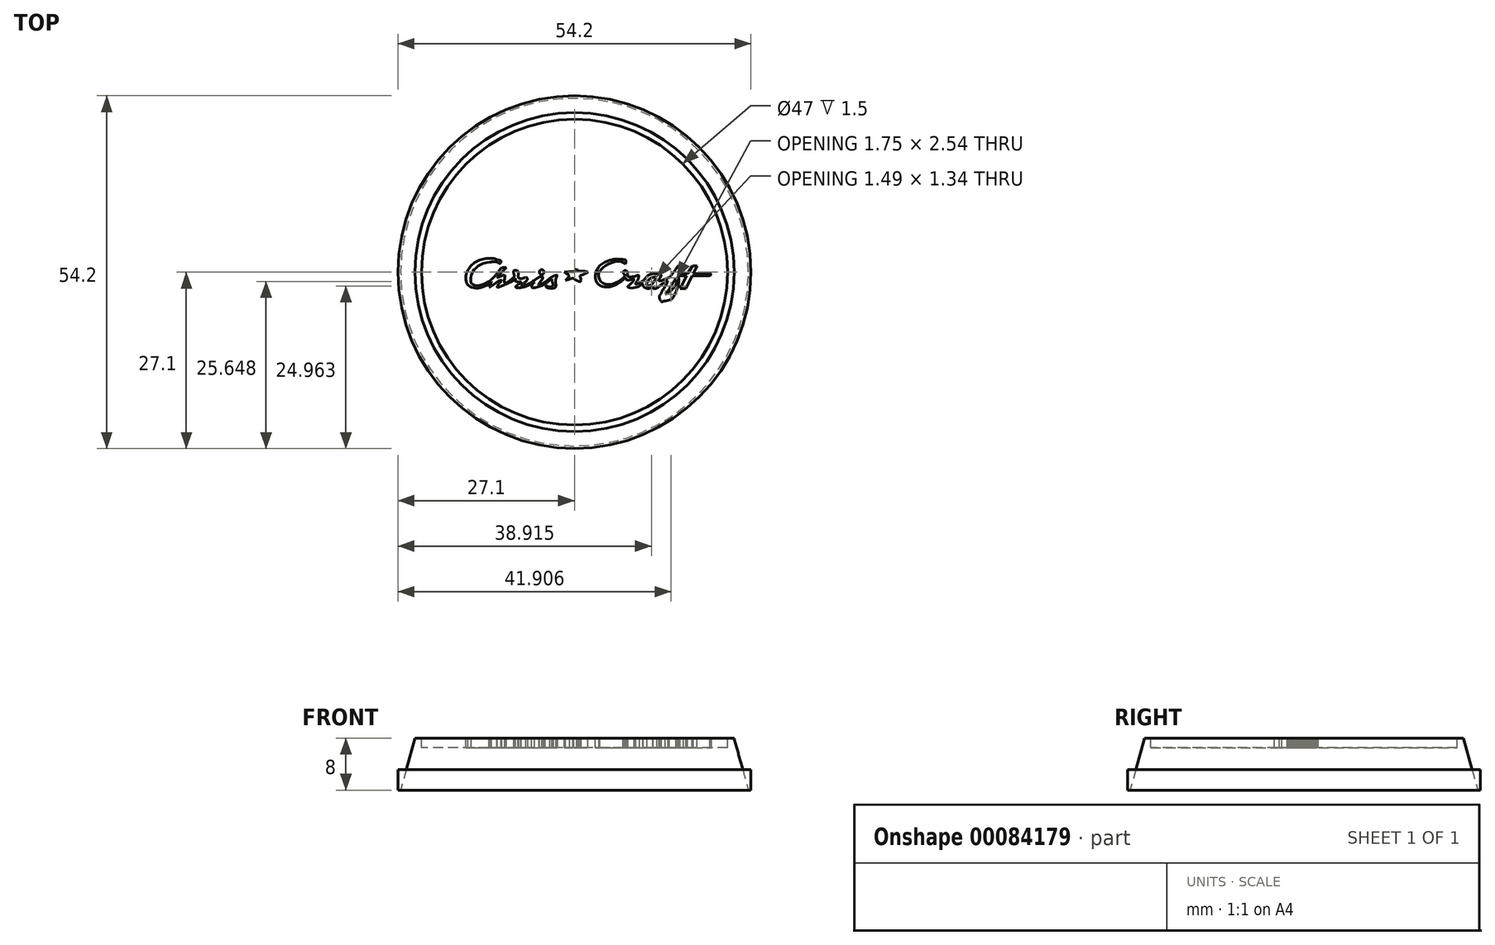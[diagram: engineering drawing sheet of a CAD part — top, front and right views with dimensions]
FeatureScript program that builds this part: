
annotation { "Feature Type Name" : "Feature", "Feature Type Description" : "" }
export const myFeature = defineFeature(function(context is Context, id is Id, definition is map)
    precondition{}
    {
        {
            var Q0;
            Q0=qCreatedBy(makeId("Top.planeOp"),FACE);
            var sketch = newSketch(context, id + "F0", { "sketchPlane" : qUnion([Q0])});
            skCircle(sketch, "E0", {"center": v(0, 0) * mm, "radius": 26.7 * mm});
            skSolve(sketch);
        }
        {
            var Q0;
            Q0=makeQuery(id+"F0.imprint","IMPRINT",FACE,{"disambiguationData":[TD([[makeQuery(id+"F0.imprint","IMPRINT",EDGE,{"derivedFrom":sQuery(id+"F0.wireOp",EDGE,"E0")}),1.0]])]});
            cPlane(context, id + "F1", {"entities" : qUnion([Q0]), "cplaneType" : CPlaneType.OFFSET, "offset" : 8 * mm, "width" : 150 * mm, "height" : 150 * mm});
        }
        {
            var Q0;
            Q0=qCreatedBy(id+"F1.planeOp",FACE);
            var sketch = newSketch(context, id + "F2", { "sketchPlane" : qUnion([Q0])});
            skCircle(sketch, "E1", {"center": v(0, 0) * mm, "radius": 24.5 * mm});
            skSolve(sketch);
        }
        {
            var Q0;
            Q0=makeQuery(id+"F0.imprint","IMPRINT",FACE,{"disambiguationData":[TD([[makeQuery(id+"F0.imprint","IMPRINT",EDGE,{"derivedFrom":sQuery(id+"F0.wireOp",EDGE,"E0")}),1.0]])]});
            var Q1;
            Q1=makeQuery(id+"F2.imprint","IMPRINT",FACE,{"disambiguationData":[TD([[makeQuery(id+"F2.imprint","IMPRINT",EDGE,{"derivedFrom":sQuery(id+"F2.wireOp",EDGE,"E1")}),1.0]])]});
            loft(context, id + "F3", {"sheetProfilesArray" : [{ "sheetProfileEntities" : qUnion([Q0]) }, { "sheetProfileEntities" : qUnion([Q1]) }]});
        }
        {
            var Q0;
            Q0=makeQuery(id+"F3.opLoft","CAP_FACE",FACE,{"disambiguationData":[OSD([makeQuery(id+"F2.imprint","IMPRINT",FACE,{"disambiguationData":[TD([[makeQuery(id+"F2.imprint","IMPRINT",EDGE,{"derivedFrom":sQuery(id+"F2.wireOp",EDGE,"E1")}),1.0]])]})])],"isStart":true});
            cPlane(context, id + "F4", {"entities" : qUnion([Q0]), "cplaneType" : CPlaneType.OFFSET, "offset" : 0 * mm, "width" : 150 * mm, "height" : 150 * mm});
        }
        {
            var Q0;
            Q0=qCreatedBy(id+"F4.planeOp",FACE);
            var sketch = newSketch(context, id + "F5", { "sketchPlane" : qUnion([Q0])});
            skCircle(sketch, "E2", {"center": v(0, 0) * mm, "radius": 23.5 * mm});
            skSolve(sketch);
        }
        {
            var Q0;
            Q0=makeQuery(id+"F5.imprint","IMPRINT",FACE,{"disambiguationData":[TD([[makeQuery(id+"F5.imprint","IMPRINT",EDGE,{"derivedFrom":sQuery(id+"F5.wireOp",EDGE,"E2")}),1.0]])]});
            extrude(context, id + "F6", {"entities" : qUnion([Q0]), "operationType" : NewBodyOperationType.REMOVE, "oppositeDirection" : true, "depth" : 1.5 * mm});
        }
        {
            var Q0;
            Q0=makeQuery(id+"F3.opLoft","CAP_FACE",FACE,{"disambiguationData":[OSD([makeQuery(id+"F0.imprint","IMPRINT",FACE,{"disambiguationData":[TD([[makeQuery(id+"F0.imprint","IMPRINT",EDGE,{"derivedFrom":sQuery(id+"F0.wireOp",EDGE,"E0")}),1.0]])]})])],"isStart":true});
            cPlane(context, id + "F7", {"entities" : qUnion([Q0]), "cplaneType" : CPlaneType.OFFSET, "offset" : 6.5 * mm, "oppositeDirection" : true, "width" : 150 * mm, "height" : 150 * mm});
        }
        {
            var Q0;
            Q0=qCreatedBy(id+"F7.planeOp",FACE);
            cPlane(context, id + "F8", {"entities" : qUnion([Q0]), "cplaneType" : CPlaneType.OFFSET, "offset" : 0 * mm, "width" : 150 * mm, "height" : 150 * mm});
        }
        {
            var Q0;
            Q0=qCreatedBy(id+"F1.planeOp",FACE);
            var sketch = newSketch(context, id + "F9", { "sketchPlane" : qUnion([Q0])});
            skPoint(sketch, "E3.end.orphan", {"position": v(217.76, 2.1) * mm});
            skFitSpline(sketch, "E4", {"points": [v(-16.36, 0.32) * mm, v(-15.75, 1.13) * mm, v(-14.75, 1.75) * mm, v(-13.66, 2.07) * mm, v(-12.5, 2.09) * mm, v(-11.62, 1.85) * mm, v(-11.25, 1.79) * mm], "startDerivative": vector(4.48, 6.5) * mm, "endDerivative": vector(2.92, -0.63) * mm});
            skFitSpline(sketch, "E5", {"points": [v(-11.25, 1.79) * mm, v(-11.45, 1.32) * mm, v(-11.8, 1.48) * mm, v(-12.14, 1.6) * mm, v(-13.06, 1.53) * mm], "startDerivative": vector(-0.58, -2.65) * mm, "endDerivative": vector(-3.08, -0.28) * mm});
            skFitSpline(sketch, "E6", {"points": [v(-16.36, 0.32) * mm, v(-16.62, -0.3) * mm, v(-16.62, -1.49) * mm, v(-16.1, -2.2) * mm, v(-14.71, -2.44) * mm, v(-13.23, -1.87) * mm, v(-12.73, -1.47) * mm], "startDerivative": vector(-2.23, -3.97) * mm, "endDerivative": vector(3.52, 2.36) * mm});
            skFitSpline(sketch, "E7", {"points": [v(-13.06, 1.53) * mm, v(-13.79, 1.4) * mm, v(-14.93, 0.83) * mm, v(-15.64, 0) * mm, v(-15.9, -0.75) * mm, v(-15.9, -1.59) * mm, v(-15.62, -1.89) * mm, v(-14.7, -2.06) * mm, v(-13.23, -1.5) * mm, v(-12.83, -1.18) * mm], "startDerivative": vector(-9.92, -1.24) * mm, "endDerivative": vector(3.94, 3.33) * mm});
            skFitSpline(sketch, "E8", {"points": [v(-12.83, -1.18) * mm, v(-11.73, 0) * mm, v(-11.25, 0.62) * mm, v(-10.44, 0.68) * mm], "startDerivative": vector(3.02, 2.92) * mm, "endDerivative": vector(3.06, -0.25) * mm});
            skFitSpline(sketch, "E9", {"points": [v(-10.44, 0.68) * mm, v(-11.19, 0) * mm, v(-11.9, -0.87) * mm], "startDerivative": vector(-1.56, -1.33) * mm, "endDerivative": vector(-1.34, -1.77) * mm});
            skFitSpline(sketch, "E10", {"points": [v(-12.73, -1.47) * mm, v(-13.11, -2.26) * mm], "startDerivative": vector(-0.49, -0.89) * mm, "endDerivative": vector(-0.49, -0.89) * mm});
            skFitSpline(sketch, "E11", {"points": [v(-13.11, -2.26) * mm, v(-12.9, -2.26) * mm, v(-11.64, -1.36) * mm, v(-11.23, -1.27) * mm, v(-11.87, -2.26) * mm, v(-9.33, -1.19) * mm], "startDerivative": vector(2.54, -0.83) * mm, "endDerivative": vector(12.1, 7) * mm});
            skFitSpline(sketch, "E12", {"points": [v(-11.9, -0.87) * mm, v(-11.17, -0.56) * mm], "startDerivative": vector(0.72, 0.31) * mm, "endDerivative": vector(0.72, 0.31) * mm});
            skFitSpline(sketch, "E13", {"points": [v(-11.17, -0.56) * mm, v(-10.7, -0.56) * mm, v(-10.75, -1.61) * mm, v(-9.74, -1.13) * mm, v(-9.18, -0.56) * mm], "startDerivative": vector(3.38, 1.13) * mm, "endDerivative": vector(1.67, 2.1) * mm});
            skFitSpline(sketch, "E14", {"points": [v(-9.18, -0.56) * mm, v(-9.32, -0.29) * mm, v(-9.32, 0.17) * mm, v(-8.84, 0.25) * mm, v(-8.64, -0.14) * mm, v(-8.68, -0.56) * mm, v(-9.03, -0.96) * mm, v(-9.33, -1.19) * mm], "startDerivative": vector(-1.19, 1.93) * mm, "endDerivative": vector(-3.2, -1.17) * mm});
            skFitSpline(sketch, "E15", {"points": [v(-8.68, -0.56) * mm, v(-8.5, -0.96) * mm, v(-7.91, -0.96) * mm, v(-7.49, -0.77) * mm], "startDerivative": vector(0.37, -1.64) * mm, "endDerivative": vector(1.59, 0.59) * mm});
            skFitSpline(sketch, "E16", {"points": [v(-7.49, -0.77) * mm, v(-7.22, -1.06) * mm, v(-7.9, -1.84) * mm, v(-8.22, -2.06) * mm], "startDerivative": vector(1.51, -0.83) * mm, "endDerivative": vector(-0.95, -0.54) * mm});
            skFitSpline(sketch, "E17", {"points": [v(-9.03, -0.96) * mm, v(-9.03, -1.42) * mm, v(-8.18, -1.55) * mm, v(-9.03, -2.22) * mm, v(-8.26, -2.4) * mm, v(-6.15, -1.52) * mm], "startDerivative": vector(-1.52, -4.12) * mm, "endDerivative": vector(6.97, 4) * mm});
            skFitSpline(sketch, "E18", {"points": [v(-8.22, -2.06) * mm, v(-8.13, -2.18) * mm, v(-7.19, -1.87) * mm, v(-6.39, -1.4) * mm, v(-5.86, -1.05) * mm, v(-5.42, -0.74) * mm, v(-5.12, -0.66) * mm, v(-4.87, -0.75) * mm, v(-5.02, -1.22) * mm], "startDerivative": vector(0.53, -2.89) * mm, "endDerivative": vector(-2.38, -4.4) * mm});
            skFitSpline(sketch, "E19.trimOffspring", {"points": [v(-9.18, -0.56) * mm, v(-9.32, -0.29) * mm, v(-9.32, 0.17) * mm, v(-8.84, 0.25) * mm, v(-8.64, -0.14) * mm, v(-8.68, -0.56) * mm, v(-9.03, -0.96) * mm, v(-9.33, -1.19) * mm], "startDerivative": vector(-1.19, 1.93) * mm, "endDerivative": vector(-3.2, -1.17) * mm});
            skFitSpline(sketch, "E20", {"points": [v(-6.15, -1.52) * mm, v(-6.54, -2.06) * mm, v(-6.49, -2.37) * mm, v(-5.58, -2.27) * mm, v(-4.46, -1.78) * mm, v(-3.82, -1.22) * mm], "startDerivative": vector(-2.62, -2.83) * mm, "endDerivative": vector(2.76, 2.7) * mm});
            skFitSpline(sketch, "E21", {"points": [v(-5.02, -1.22) * mm, v(-5.51, -1.95) * mm, v(-4.88, -1.76) * mm, v(-3.93, -1.1) * mm, v(-3.47, -0.75) * mm, v(-3.16, -0.57) * mm, v(-2.9, -0.5) * mm, v(-2.68, -0.5) * mm, v(-2.77, -0.81) * mm, v(-2.91, -1.22) * mm, v(-2.86, -2.06) * mm, v(-3.06, -2.46) * mm, v(-4, -2.46) * mm, v(-4.48, -2.06) * mm], "startDerivative": vector(-8.62, -10.22) * mm, "endDerivative": vector(-4.69, 5.4) * mm});
            skFitSpline(sketch, "E22", {"points": [v(-4.48, -2.06) * mm, v(-3.7, -2.27) * mm, v(-3.32, -2.06) * mm, v(-3.42, -1.46) * mm, v(-3.5, -1.04) * mm], "startDerivative": vector(2.72, -0.78) * mm, "endDerivative": vector(-0.08, 1.69) * mm});
            skFitSpline(sketch, "E23", {"points": [v(-3.82, -1.22) * mm, v(-3.5, -1.04) * mm], "startDerivative": vector(0.33, 0.18) * mm, "endDerivative": vector(0.33, 0.18) * mm});
            skCircle(sketch, "E24", {"center": v(-5.04, 0) * mm, "radius": 0.37 * mm});
            skLineSegment(sketch, "E25", {"start": v(-1.4, -1.28) * mm, "end": v(-0.74, -0.58) * mm});
            skFitSpline(sketch, "E26", {"points": [v(0.33, 0.53) * mm, v(0.95, -1.45) * mm, v(-1.55, 0) * mm], "startDerivative": vector(2.73, -5.92) * mm, "endDerivative": vector(-6.23, 4.57) * mm});
            skFitSpline(sketch, "E27", {"points": [v(-1.55, 0) * mm, v(2, 0) * mm, v(-1.4, -1.28) * mm], "startDerivative": vector(10.62, 0.63) * mm, "endDerivative": vector(-10.3, -3.2) * mm});
            skFitSpline(sketch, "E28", {"points": [v(3.9, 1) * mm, v(5.07, 1.69) * mm, v(5.95, 1.96) * mm, v(6.8, 2) * mm, v(7.92, 1.86) * mm], "startDerivative": vector(5.12, 4.38) * mm, "endDerivative": vector(4.47, -0.85) * mm});
            skFitSpline(sketch, "E29", {"points": [v(3.9, 1) * mm, v(3.25, -0.27) * mm, v(3.28, -1.28) * mm, v(3.9, -2.04) * mm, v(5.46, -2.25) * mm, v(7.13, -1.45) * mm, v(7.76, -0.81) * mm], "startDerivative": vector(-5.62, -6.37) * mm, "endDerivative": vector(3.23, 4.65) * mm});
            skFitSpline(sketch, "E30", {"points": [v(7.92, 1.86) * mm, v(7.81, 1.24) * mm], "startDerivative": vector(-0.34, -0.66) * mm, "endDerivative": vector(-0.34, -0.66) * mm});
            skFitSpline(sketch, "E31", {"points": [v(7.81, 1.24) * mm, v(7.52, 1.44) * mm, v(7.08, 1.62) * mm, v(6.4, 1.62) * mm, v(5.18, 1.24) * mm, v(4.45, 0.74) * mm, v(3.92, 0.18) * mm, v(3.7, -0.53) * mm, v(3.9, -1.27) * mm, v(4.57, -1.82) * mm, v(5.71, -1.86) * mm, v(6.72, -1.46) * mm, v(7.44, -0.91) * mm], "startDerivative": vector(-5.15, 2.9) * mm, "endDerivative": vector(8.52, 6.43) * mm});
            skFitSpline(sketch, "E32", {"points": [v(7.44, -0.91) * mm, v(7.67, -0.66) * mm, v(7.72, -0.3) * mm, v(7.67, -0.12) * mm], "startDerivative": vector(0.71, 0.62) * mm, "endDerivative": vector(-0.27, 0.56) * mm});
            skFitSpline(sketch, "E33", {"points": [v(7.72, -0.3) * mm, v(7.55, -0.22) * mm, v(7.48, 0) * mm, v(7.6, 0.16) * mm, v(7.72, 0.25) * mm, v(8.06, 0.11) * mm, v(8.18, -0.23) * mm], "startDerivative": vector(-1.25, 0.27) * mm, "endDerivative": vector(0.19, -1.64) * mm});
            skPoint(sketch, "E34.5.internal.snap0", {"position": v(8.22, -2.02) * mm});
            skFitSpline(sketch, "E34", {"points": [v(7.76, -0.81) * mm, v(8, -1.2) * mm, v(8.8, -1.14) * mm, v(9.15, -1.1) * mm, v(8.7, -1.73) * mm, v(8.22, -2.3) * mm, v(9.17, -2.4) * mm, v(10.02, -2.09) * mm], "startDerivative": vector(1.28, -4.05) * mm, "endDerivative": vector(1.85, 2.26) * mm});
            skLineSegment(sketch, "E35.trimOffspring", {"start": v(-0.1, 0.08) * mm, "end": v(0.33, 0.53) * mm});
            skFitSpline(sketch, "E36.trimOffspring", {"points": [v(0.33, 0.53) * mm, v(0.95, -1.45) * mm, v(-1.55, 0) * mm], "startDerivative": vector(2.73, -5.92) * mm, "endDerivative": vector(-6.23, 4.57) * mm});
            skLineSegment(sketch, "E37.trimOffspring", {"start": v(-0.25, -0.92) * mm, "end": v(-0.25, -0.92) * mm});
            skFitSpline(sketch, "E38", {"points": [v(8.18, -0.23) * mm, v(8.18, -0.65) * mm, v(8.96, -0.71) * mm, v(9.54, -0.56) * mm, v(9.86, -0.5) * mm, v(9.67, -1.3) * mm, v(9.35, -1.85) * mm, v(10.52, -1.4) * mm], "startDerivative": vector(-1.2, -4.34) * mm, "endDerivative": vector(8.48, 4.05) * mm});
            skFitSpline(sketch, "E39", {"points": [v(10.52, -1.4) * mm, v(10.84, -0.97) * mm, v(11.23, -0.56) * mm, v(11.6, -0.34) * mm, v(12.1, -0.24) * mm, v(12.52, -0.22) * mm, v(13.13, -0.3) * mm], "startDerivative": vector(1.8, 2.48) * mm, "endDerivative": vector(3.52, -0.49) * mm});
            skFitSpline(sketch, "E40", {"points": [v(10.02, -2.09) * mm, v(10.54, -1.78) * mm], "startDerivative": vector(0.52, 0.3) * mm, "endDerivative": vector(0.52, 0.3) * mm});
            skFitSpline(sketch, "E41", {"points": [v(10.54, -1.78) * mm, v(10.54, -2.1) * mm, v(10.91, -2.43) * mm, v(11.52, -2.51) * mm, v(12.08, -2.2) * mm], "startDerivative": vector(-0.32, -1.66) * mm, "endDerivative": vector(1.92, 1.4) * mm});
            skFitSpline(sketch, "E42", {"points": [v(13.13, -0.3) * mm, v(13.27, -0.44) * mm, v(13.13, -0.88) * mm, v(12.9, -1.33) * mm, v(13.4, -1.3) * mm, v(13.81, -1.1) * mm, v(14.54, -0.82) * mm], "startDerivative": vector(1.54, -1.11) * mm, "endDerivative": vector(3.13, 1.13) * mm});
            skFitSpline(sketch, "E43", {"points": [v(12.08, -2.2) * mm, v(12.08, -2.51) * mm, v(12.47, -2.51) * mm, v(13.15, -2.07) * mm, v(13.76, -1.61) * mm, v(14.37, -1.3) * mm], "startDerivative": vector(-0.56, -2.5) * mm, "endDerivative": vector(2.52, 1.6) * mm});
            skFitSpline(sketch, "E44", {"points": [v(14.54, -0.82) * mm, v(15.44, 0.29) * mm, v(15.9, 0.98) * mm], "startDerivative": vector(2.06, 2.12) * mm, "endDerivative": vector(0.93, 1.58) * mm});
            skFitSpline(sketch, "E45", {"points": [v(15.9, 0.98) * mm, v(16.71, 0.98) * mm], "startDerivative": vector(0.81, 0) * mm, "endDerivative": vector(0.81, 0) * mm});
            skFitSpline(sketch, "E46", {"points": [v(14.37, -1.3) * mm, v(13.93, -2.14) * mm, v(13.39, -3.06) * mm, v(13.02, -3.77) * mm], "startDerivative": vector(-1.26, -2.37) * mm, "endDerivative": vector(-1.17, -2.19) * mm});
            skFitSpline(sketch, "E47", {"points": [v(16.71, 0.98) * mm, v(16.27, 0.3) * mm, v(15.98, -0.22) * mm], "startDerivative": vector(-0.85, -1.32) * mm, "endDerivative": vector(-0.7, -1.05) * mm});
            skFitSpline(sketch, "E48", {"points": [v(15.98, -0.22) * mm, v(22.19, -0.22) * mm], "startDerivative": vector(6.26, -0.17) * mm, "endDerivative": vector(6.27, 0.1) * mm});
            skFitSpline(sketch, "E49", {"points": [v(15.98, -0.22) * mm, v(14.6, -2.48) * mm, v(13.93, -3.4) * mm], "startDerivative": vector(-2.37, -4.2) * mm, "endDerivative": vector(-1.58, -2.05) * mm});
            skFitSpline(sketch, "E50", {"points": [v(13.93, -3.4) * mm, v(14.56, -3.02) * mm, v(15.2, -2.45) * mm, v(15.66, -1.72) * mm, v(15.6, -0.87) * mm], "startDerivative": vector(2.7, 1.52) * mm, "endDerivative": vector(-0.89, 3.54) * mm});
            skFitSpline(sketch, "E51", {"points": [v(13.02, -3.77) * mm, v(13.12, -4.22) * mm, v(13.37, -4.56) * mm], "startDerivative": vector(0.11, -0.93) * mm, "endDerivative": vector(0.6, -0.65) * mm});
            skFitSpline(sketch, "E52", {"points": [v(13.37, -4.56) * mm, v(13.7, -4.46) * mm, v(14.85, -4.16) * mm, v(15.62, -2.88) * mm, v(15.97, -1.85) * mm, v(15.94, -0.58) * mm], "startDerivative": vector(2.45, 0.31) * mm, "endDerivative": vector(-0.67, 5.74) * mm});
            skLineSegment(sketch, "E53", {"start": v(15.94, -0.58) * mm, "end": v(17.25, -0.58) * mm});
            skLineSegment(sketch, "E54", {"start": v(20.8, -0.58) * mm, "end": v(21.06, -0.23) * mm});
            skFitSpline(sketch, "E55", {"points": [v(12.3, -0.78) * mm, v(11.87, -0.84) * mm, v(11.46, -1.1) * mm, v(11.17, -1.54) * mm, v(11.07, -1.98) * mm, v(11.46, -2.12) * mm, v(11.97, -1.73) * mm, v(12.31, -1.26) * mm, v(12.54, -0.93) * mm, v(12.56, -0.78) * mm, v(12.3, -0.78) * mm]});
            skLineSegment(sketch, "E56.trimOffspring", {"start": v(18.05, -0.58) * mm, "end": v(20.8, -0.58) * mm});
            skLineSegment(sketch, "E57", {"start": v(17.37, -0.24) * mm, "end": v(18.09, 0.96) * mm});
            skLineSegment(sketch, "E58", {"start": v(18.09, 0.96) * mm, "end": v(18.81, 0.96) * mm});
            skLineSegment(sketch, "E59", {"start": v(17.25, -0.58) * mm, "end": v(16.22, -2.53) * mm});
            skLineSegment(sketch, "E60", {"start": v(16.22, -2.53) * mm, "end": v(17.1, -2.53) * mm});
            skLineSegment(sketch, "E61", {"start": v(17.1, -2.53) * mm, "end": v(18.05, -0.58) * mm});
            skLineSegment(sketch, "E62.trimOffspring", {"start": v(18.22, -0.25) * mm, "end": v(18.81, 0.96) * mm});
            skLineSegment(sketch, "E63", {"start": v(-1.4, -1.28) * mm, "end": v(-0.25, -0.92) * mm});
            skLineSegment(sketch, "E64", {"start": v(-0.74, -0.58) * mm, "end": v(-1.55, 0) * mm});
            skSolve(sketch);
        }
        {
            var Q0;
            Q0 = qSketchRegion(id + "F9", true);
            var Q1;
            Q1=qCreatedBy(id+"F8.planeOp",FACE);
            extrude(context, id + "F10", {"entities" : qUnion([Q0]), "endBound" : BoundingType.UP_TO_SURFACE, "oppositeDirection" : true, "endBoundEntityFace" : qUnion([Q1]), "depth" : 2 * mm});
        }
        {
            var Q0;
            Q0=qCreatedBy(id+"F1.planeOp",FACE);
            cPlane(context, id + "F11", {"entities" : qUnion([Q0]), "cplaneType" : CPlaneType.OFFSET, "offset" : 8 * mm, "oppositeDirection" : true, "width" : 150 * mm, "height" : 150 * mm});
        }
        {
            var Q0;
            Q0=qCreatedBy(id+"F11.planeOp",FACE);
            var sketch = newSketch(context, id + "F12", { "sketchPlane" : qUnion([Q0])});
            skCircle(sketch, "E65", {"center": v(0, 0) * mm, "radius": 27.1 * mm});
            skSolve(sketch);
        }
        {
            var Q0;
            Q0 = qSketchRegion(id + "F12", true);
            var Q1;
            Q1 = qConstructionFilter(qBodyType(qCreatedBy(id + "F12" ,EDGE), BodyType.WIRE), ConstructionObject.NO);
            extrude(context, id + "F13", {"entities" : qUnion([Q0]), "surfaceEntities" : qUnion([Q1]), "depth" : 3.17 * mm});
        }
    });
